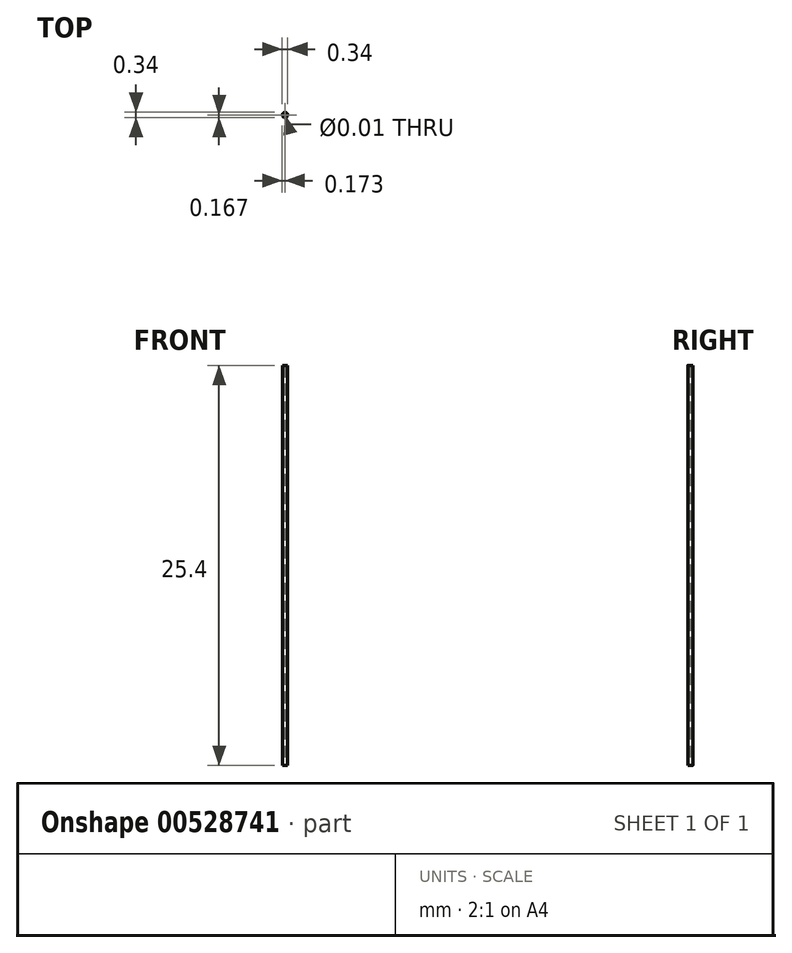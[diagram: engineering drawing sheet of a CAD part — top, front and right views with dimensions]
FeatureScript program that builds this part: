
annotation { "Feature Type Name" : "Feature", "Feature Type Description" : "" }
export const myFeature = defineFeature(function(context is Context, id is Id, definition is map)
    precondition{}
    {
        {
            var Q0;
            Q0=qCreatedBy(makeId("Top.planeOp"),FACE);
            var sketch = newSketch(context, id + "F0", { "sketchPlane" : qUnion([Q0])});
            skCircle(sketch, "E0", {"center": v(-26.09, 1.47) * mm, "radius": 0 * mm});
            skCircle(sketch, "E1", {"center": v(-26.09, 1.47) * mm, "radius": 0.17 * mm});
            skSolve(sketch);
        }
        {
            var Q0;
            Q0 = qSketchRegion(id + "F0", true);
            extrude(context, id + "F1", {"entities" : qUnion([Q0]), "depth" : 25.4 * mm, "offsetDistance" : 25.4 * mm});
        }
    });
